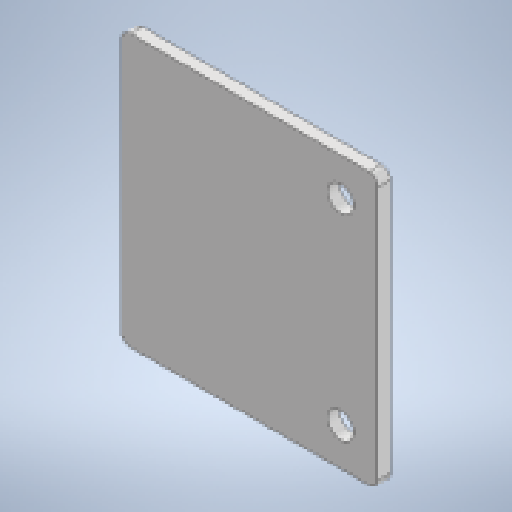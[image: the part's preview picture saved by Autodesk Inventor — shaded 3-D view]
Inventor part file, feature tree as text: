
AUTODESK INVENTOR PART (.ipt)
format: ipt  version: 2025 (Build 290162010, 162A)  size: 157,696 bytes
history: native  units: mm
features: sketch x2, sheet_metal_op x1, hole x1, chamfer x1, mirror x1, other x1
ambient origin geometry x8: Origin, YZ Plane, XZ Plane, XY Plane, X Axis, Y Axis, Z Axis, Center Point
bodies: Solid1 (feature_tree)
feature tree (7):
  sheet_metal_op  "Face1"
  hole  "Hole1"  [1 undecoded]
  chamfer  "Corner Round1"
  mirror  "Mirror1"
  sketch  "Sketch1"  dims[d0=180.0mm d1=180.0mm]
  other  "Plate1"
  sketch  "Sketch2"  dims[d2=8.0mm d3=17.0mm d4=6.0mm d5=4.0mm d6=2.0mm d7=90.0deg d8=8.0mm d9=20.594885mm d10=25.0mm d12=25.0mm d13=6.0mm]
note: 1 required parameter value undecoded (feature->parameter linkage not recoverable at this tier; creation-order binding heuristic only, values carry confidence <= 0.55)
